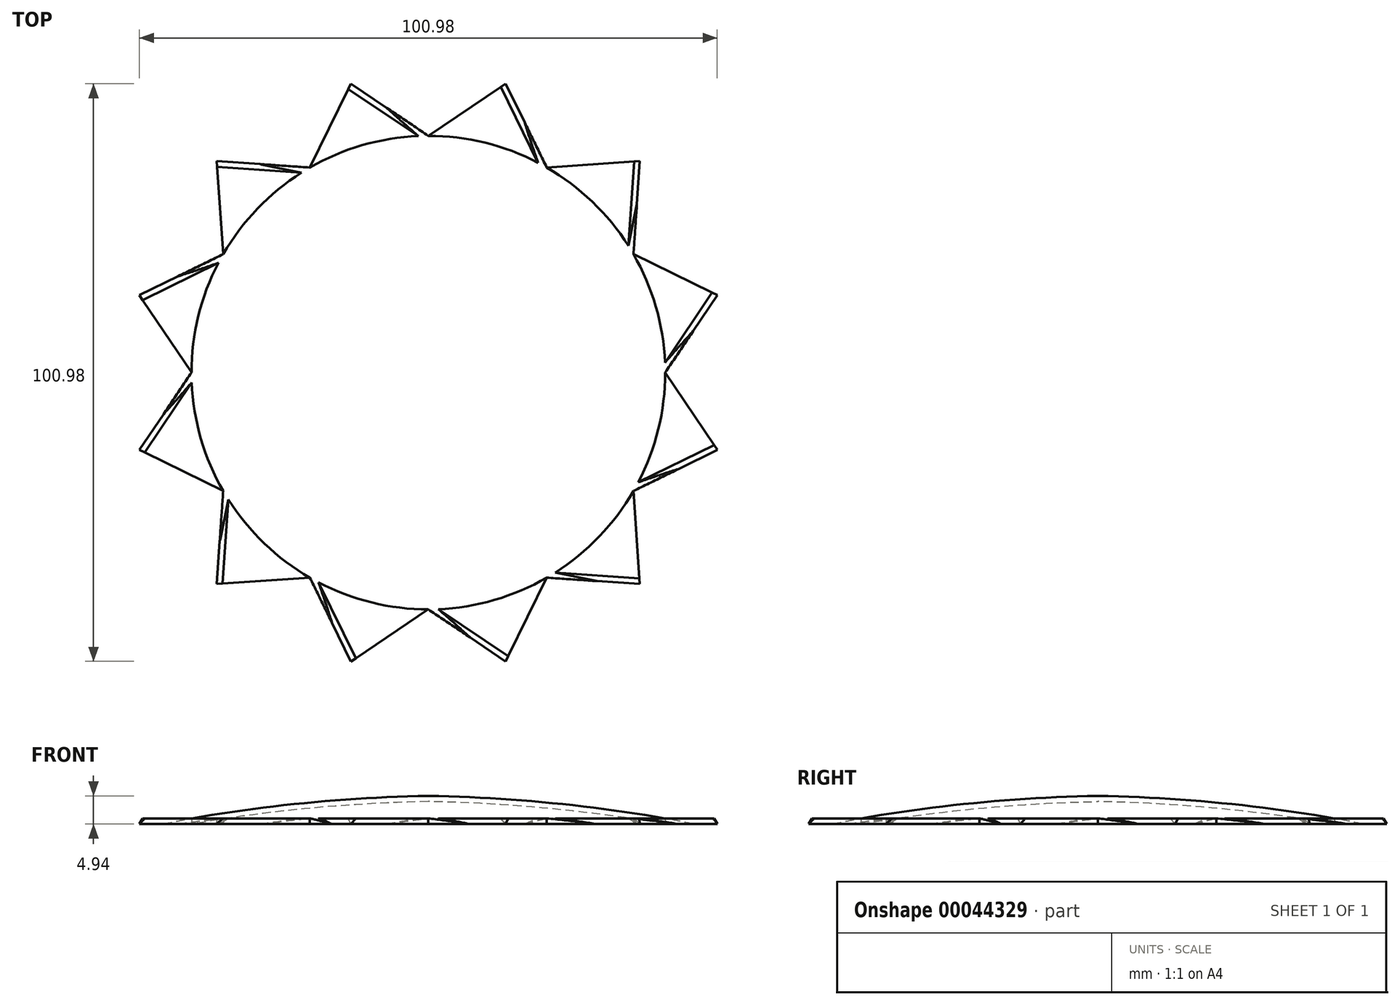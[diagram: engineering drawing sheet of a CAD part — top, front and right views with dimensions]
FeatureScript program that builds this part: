
annotation { "Feature Type Name" : "Feature", "Feature Type Description" : "" }
export const myFeature = defineFeature(function(context is Context, id is Id, definition is map)
    precondition{}
    {
        {
            var Q0;
            Q0=qCreatedBy(makeId("Front.planeOp"),FACE);
            var sketch = newSketch(context, id + "F0", { "sketchPlane" : qUnion([Q0])});
            skLineSegment(sketch, "E0", {"start": v(0, 4.94) * mm, "end": v(0, 3.94) * mm});
            skLineSegment(sketch, "E1", {"start": v(-41.4, 1) * mm, "end": v(-41.4, 0) * mm});
            skLineSegment(sketch, "E2", {"start": v(-41.4, 0) * mm, "end": v(0, 0) * mm, "construction": true});
            skArc(sketch, "E3", {"start": v(0, 3.94) * mm, "mid": v(-20.77, 2.76) * mm, "end": v(-41.4, 0) * mm});
            skArc(sketch, "E4", {"start": v(0, 4.94) * mm, "mid": v(-20.77, 3.76) * mm, "end": v(-41.4, 1) * mm});
            skSolve(sketch);
        }
        {
            var Q0;
            Q0=makeQuery(id+"F0.imprint","IMPRINT",FACE,{"disambiguationData":[TD([[makeQuery(id+"F0.imprint","IMPRINT",EDGE,{"derivedFrom":sQuery(id+"F0.wireOp",EDGE,"E0")}),-1.0]])]});
            var Q1;
            Q1=sQuery(id+"F0.wireOp",EDGE,"E0");
            revolve(context, id + "F1", {"entities" : qUnion([Q0]), "axis" : qUnion([Q1]), "revolveType" : RevolveType.FULL});
        }
        {
            var Q0;
            Q0=qCreatedBy(makeId("Top.planeOp"),FACE);
            var sketch = newSketch(context, id + "F2", { "sketchPlane" : qUnion([Q0])});
            skCircle(sketch, "E5", {"center": v(0, 0) * mm, "radius": 41.4 * mm});
            skLineSegment(sketch, "E6", {"start": v(0, 0) * mm, "end": v(31.94, 26.33) * mm, "construction": true});
            skLineSegment(sketch, "E7", {"start": v(0, 41.4) * mm, "end": v(13.53, 50.5) * mm});
            skLineSegment(sketch, "E8", {"start": v(13.53, 50.5) * mm, "end": v(20.7, 35.85) * mm});
            skLineSegment(sketch, "E9", {"start": v(20.7, 35.85) * mm, "end": v(36.96, 36.96) * mm});
            skLineSegment(sketch, "E10", {"start": v(36.96, 36.96) * mm, "end": v(35.85, 20.7) * mm});
            skLineSegment(sketch, "E11", {"start": v(35.85, 20.7) * mm, "end": v(50.5, 13.53) * mm});
            skLineSegment(sketch, "E12", {"start": v(50.5, 13.53) * mm, "end": v(41.4, 0) * mm});
            skLineSegment(sketch, "E13", {"start": v(0, 41.4) * mm, "end": v(20.7, 35.85) * mm, "construction": true});
            skLineSegment(sketch, "E14", {"start": v(20.7, 35.85) * mm, "end": v(35.85, 20.7) * mm, "construction": true});
            skLineSegment(sketch, "E15", {"start": v(35.85, 20.7) * mm, "end": v(41.4, 0) * mm, "construction": true});
            skLineSegment(sketch, "E16", {"start": v(41.4, 0) * mm, "end": v(50.5, -13.53) * mm});
            skLineSegment(sketch, "E17", {"start": v(50.5, -13.53) * mm, "end": v(35.85, -20.7) * mm});
            skLineSegment(sketch, "E18", {"start": v(35.85, -20.7) * mm, "end": v(36.96, -36.96) * mm});
            skLineSegment(sketch, "E19", {"start": v(36.96, -36.96) * mm, "end": v(20.7, -35.85) * mm});
            skLineSegment(sketch, "E20", {"start": v(20.7, -35.85) * mm, "end": v(13.53, -50.5) * mm});
            skLineSegment(sketch, "E21", {"start": v(13.53, -50.5) * mm, "end": v(0, -41.4) * mm});
            skLineSegment(sketch, "E22", {"start": v(41.4, 0) * mm, "end": v(35.85, -20.7) * mm, "construction": true});
            skLineSegment(sketch, "E23", {"start": v(35.85, -20.7) * mm, "end": v(20.7, -35.85) * mm, "construction": true});
            skLineSegment(sketch, "E24", {"start": v(20.7, -35.85) * mm, "end": v(0, -41.4) * mm, "construction": true});
            skLineSegment(sketch, "E25", {"start": v(0, -41.4) * mm, "end": v(-13.53, -50.5) * mm});
            skLineSegment(sketch, "E26", {"start": v(-13.53, -50.5) * mm, "end": v(-20.7, -35.85) * mm});
            skLineSegment(sketch, "E27", {"start": v(-20.7, -35.85) * mm, "end": v(-36.96, -36.96) * mm});
            skLineSegment(sketch, "E28", {"start": v(-36.96, -36.96) * mm, "end": v(-35.85, -20.7) * mm});
            skLineSegment(sketch, "E29", {"start": v(-35.85, -20.7) * mm, "end": v(-50.5, -13.53) * mm});
            skLineSegment(sketch, "E30", {"start": v(-50.5, -13.53) * mm, "end": v(-41.4, 0) * mm});
            skLineSegment(sketch, "E31", {"start": v(-41.4, 0) * mm, "end": v(-35.85, -20.7) * mm, "construction": true});
            skLineSegment(sketch, "E32", {"start": v(-35.85, -20.7) * mm, "end": v(-20.7, -35.85) * mm, "construction": true});
            skLineSegment(sketch, "E33", {"start": v(-20.7, -35.85) * mm, "end": v(0, -41.4) * mm, "construction": true});
            skLineSegment(sketch, "E34", {"start": v(-41.4, 0) * mm, "end": v(-50.5, 13.53) * mm});
            skLineSegment(sketch, "E35", {"start": v(-50.5, 13.53) * mm, "end": v(-35.85, 20.7) * mm});
            skLineSegment(sketch, "E36", {"start": v(-35.85, 20.7) * mm, "end": v(-36.96, 36.96) * mm});
            skLineSegment(sketch, "E37", {"start": v(-36.96, 36.96) * mm, "end": v(-20.7, 35.85) * mm});
            skLineSegment(sketch, "E38", {"start": v(-20.7, 35.85) * mm, "end": v(-13.53, 50.5) * mm});
            skLineSegment(sketch, "E39", {"start": v(-13.53, 50.5) * mm, "end": v(0, 41.4) * mm});
            skLineSegment(sketch, "E40", {"start": v(-41.4, 0) * mm, "end": v(-35.85, 20.7) * mm, "construction": true});
            skLineSegment(sketch, "E41", {"start": v(-35.85, 20.7) * mm, "end": v(-20.7, 35.85) * mm, "construction": true});
            skLineSegment(sketch, "E42", {"start": v(-20.7, 35.85) * mm, "end": v(0, 41.4) * mm, "construction": true});
            skSolve(sketch);
        }
        {
            var Q0;
            {var subQ0=sQuery(id+"F2.wireOp",EDGE,"E7");Q0=makeQuery(id+"F2.imprint","IMPRINT",FACE,{"disambiguationData":[TD([[makeQuery(id+"F2.imprint","IMPRINT",EDGE,{"derivedFrom":subQ0}),-1.0]])]});}
            var Q1;
            {var subQ1=sQuery(id+"F2.wireOp",EDGE,"E9");Q1=makeQuery(id+"F2.imprint","IMPRINT",FACE,{"disambiguationData":[TD([[makeQuery(id+"F2.imprint","IMPRINT",EDGE,{"derivedFrom":subQ1}),-1.0]])]});}
            var Q2;
            {var subQ1=sQuery(id+"F2.wireOp",EDGE,"E11");Q2=makeQuery(id+"F2.imprint","IMPRINT",FACE,{"disambiguationData":[TD([[makeQuery(id+"F2.imprint","IMPRINT",EDGE,{"derivedFrom":subQ1}),-1.0]])]});}
            var Q3;
            {var subQ1=sQuery(id+"F2.wireOp",EDGE,"E16");Q3=makeQuery(id+"F2.imprint","IMPRINT",FACE,{"disambiguationData":[TD([[makeQuery(id+"F2.imprint","IMPRINT",EDGE,{"derivedFrom":subQ1}),-1.0]])]});}
            var Q4;
            {var subQ1=sQuery(id+"F2.wireOp",EDGE,"E18");Q4=makeQuery(id+"F2.imprint","IMPRINT",FACE,{"disambiguationData":[TD([[makeQuery(id+"F2.imprint","IMPRINT",EDGE,{"derivedFrom":subQ1}),-1.0]])]});}
            var Q5;
            {var subQ1=sQuery(id+"F2.wireOp",EDGE,"E20");Q5=makeQuery(id+"F2.imprint","IMPRINT",FACE,{"disambiguationData":[TD([[makeQuery(id+"F2.imprint","IMPRINT",EDGE,{"derivedFrom":subQ1}),-1.0]])]});}
            var Q6;
            {var subQ1=sQuery(id+"F2.wireOp",EDGE,"E25");Q6=makeQuery(id+"F2.imprint","IMPRINT",FACE,{"disambiguationData":[TD([[makeQuery(id+"F2.imprint","IMPRINT",EDGE,{"derivedFrom":subQ1}),-1.0]])]});}
            var Q7;
            {var subQ1=sQuery(id+"F2.wireOp",EDGE,"E27");Q7=makeQuery(id+"F2.imprint","IMPRINT",FACE,{"disambiguationData":[TD([[makeQuery(id+"F2.imprint","IMPRINT",EDGE,{"derivedFrom":subQ1}),-1.0]])]});}
            var Q8;
            {var subQ1=sQuery(id+"F2.wireOp",EDGE,"E29");Q8=makeQuery(id+"F2.imprint","IMPRINT",FACE,{"disambiguationData":[TD([[makeQuery(id+"F2.imprint","IMPRINT",EDGE,{"derivedFrom":subQ1}),-1.0]])]});}
            var Q9;
            {var subQ1=sQuery(id+"F2.wireOp",EDGE,"E34");Q9=makeQuery(id+"F2.imprint","IMPRINT",FACE,{"disambiguationData":[TD([[makeQuery(id+"F2.imprint","IMPRINT",EDGE,{"derivedFrom":subQ1}),-1.0]])]});}
            var Q10;
            {var subQ1=sQuery(id+"F2.wireOp",EDGE,"E36");Q10=makeQuery(id+"F2.imprint","IMPRINT",FACE,{"disambiguationData":[TD([[makeQuery(id+"F2.imprint","IMPRINT",EDGE,{"derivedFrom":subQ1}),-1.0]])]});}
            var Q11;
            {var subQ1=sQuery(id+"F2.wireOp",EDGE,"E38");Q11=makeQuery(id+"F2.imprint","IMPRINT",FACE,{"disambiguationData":[TD([[makeQuery(id+"F2.imprint","IMPRINT",EDGE,{"derivedFrom":subQ1}),-1.0]])]});}
            extrude(context, id + "F3", {"entities" : qUnion([Q0, Q1, Q2, Q3, Q4, Q5, Q6, Q7, Q8, Q9, Q10, Q11]), "operationType" : NewBodyOperationType.ADD, "depth" : 1 * mm});
        }
        {
            var Q0;
            Q0=makeQuery(id+"F3.opExtrude","CAP_EDGE",EDGE,{"disambiguationData":[OSD([sQuery(id+"F2.wireOp",EDGE,"E26")])],"isStart":false});
            var Q1;
            Q1=makeQuery(id+"F3.opExtrude","CAP_EDGE",EDGE,{"disambiguationData":[OSD([sQuery(id+"F2.wireOp",EDGE,"E21")])],"isStart":false});
            var Q2;
            Q2=makeQuery(id+"F3.opExtrude","CAP_EDGE",EDGE,{"disambiguationData":[OSD([sQuery(id+"F2.wireOp",EDGE,"E19")])],"isStart":false});
            var Q3;
            Q3=makeQuery(id+"F3.opExtrude","CAP_EDGE",EDGE,{"disambiguationData":[OSD([sQuery(id+"F2.wireOp",EDGE,"E17")])],"isStart":false});
            var Q4;
            Q4=makeQuery(id+"F3.opExtrude","CAP_EDGE",EDGE,{"disambiguationData":[OSD([sQuery(id+"F2.wireOp",EDGE,"E12")])],"isStart":false});
            var Q5;
            Q5=makeQuery(id+"F3.opExtrude","CAP_EDGE",EDGE,{"disambiguationData":[OSD([sQuery(id+"F2.wireOp",EDGE,"E10")])],"isStart":false});
            var Q6;
            Q6=makeQuery(id+"F3.opExtrude","CAP_EDGE",EDGE,{"disambiguationData":[OSD([sQuery(id+"F2.wireOp",EDGE,"E8")])],"isStart":false});
            var Q7;
            Q7=makeQuery(id+"F3.opExtrude","CAP_EDGE",EDGE,{"disambiguationData":[OSD([sQuery(id+"F2.wireOp",EDGE,"E39")])],"isStart":false});
            var Q8;
            Q8=makeQuery(id+"F3.opExtrude","CAP_EDGE",EDGE,{"disambiguationData":[OSD([sQuery(id+"F2.wireOp",EDGE,"E37")])],"isStart":false});
            var Q9;
            Q9=makeQuery(id+"F3.opExtrude","CAP_EDGE",EDGE,{"disambiguationData":[OSD([sQuery(id+"F2.wireOp",EDGE,"E35")])],"isStart":false});
            var Q10;
            Q10=makeQuery(id+"F3.opExtrude","CAP_EDGE",EDGE,{"disambiguationData":[OSD([sQuery(id+"F2.wireOp",EDGE,"E30")])],"isStart":false});
            var Q11;
            Q11=makeQuery(id+"F3.opExtrude","CAP_EDGE",EDGE,{"disambiguationData":[OSD([sQuery(id+"F2.wireOp",EDGE,"E28")])],"isStart":false});
            chamfer(context, id + "F4", {"entities" : qUnion([Q0, Q1, Q2, Q3, Q4, Q5, Q6, Q7, Q8, Q9, Q10, Q11]), "width" : 1 * mm, "tangentPropagation" : true});
        }
    });
